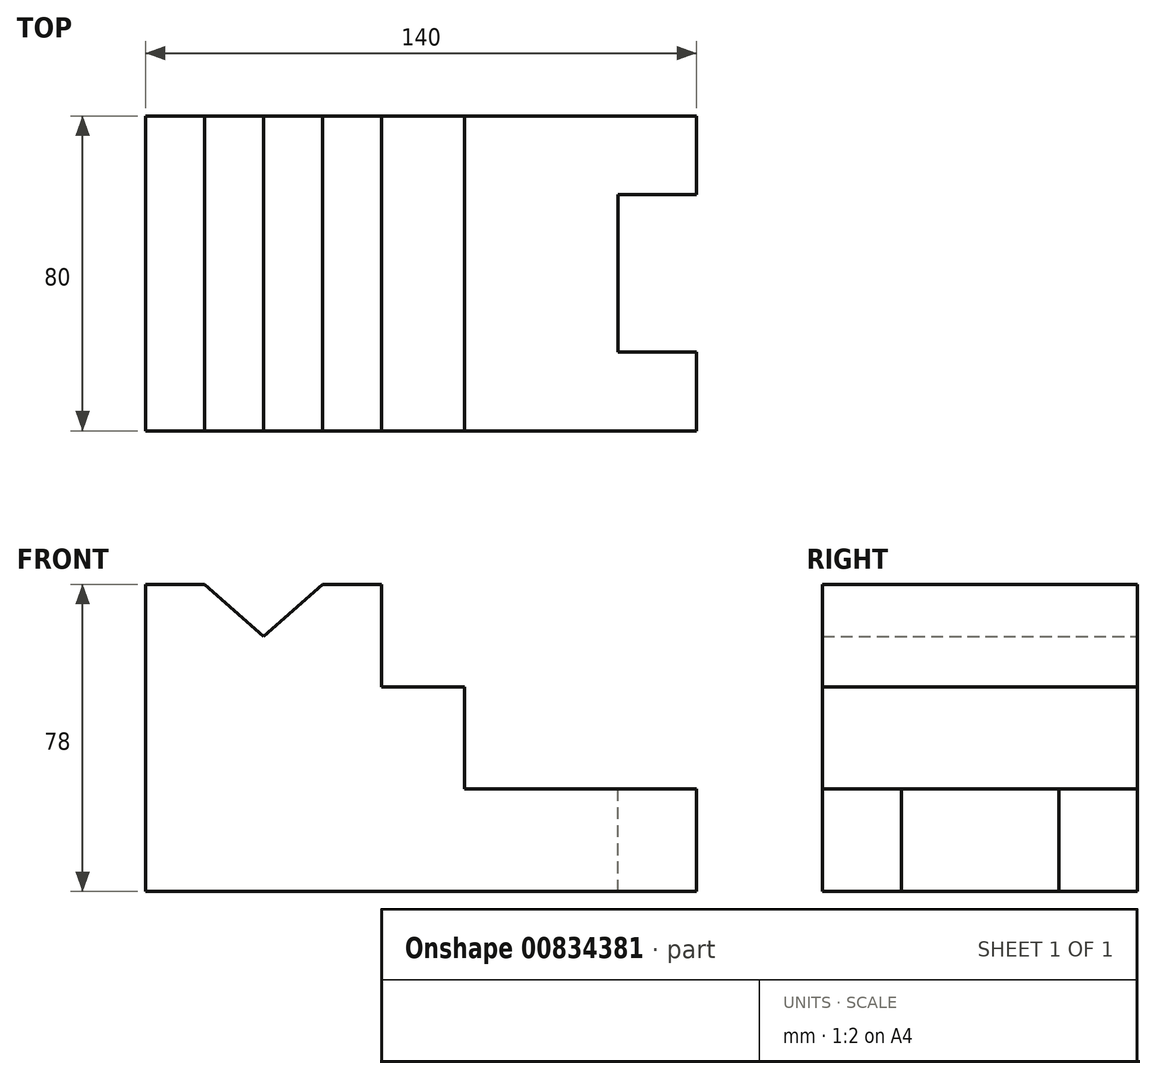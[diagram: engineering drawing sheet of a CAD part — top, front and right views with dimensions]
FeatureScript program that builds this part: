
annotation { "Feature Type Name" : "Feature", "Feature Type Description" : "" }
export const myFeature = defineFeature(function(context is Context, id is Id, definition is map)
    precondition{}
    {
        {
            var Q0;
            Q0=qCreatedBy(makeId("Front.planeOp"),FACE);
            var sketch = newSketch(context, id + "F0", { "sketchPlane" : qUnion([Q0])});
            skLineSegment(sketch, "E0", {"start": v(57.57, -14.86) * mm, "end": v(-82.43, -14.86) * mm});
            skLineSegment(sketch, "E1", {"start": v(-82.43, -14.86) * mm, "end": v(-82.43, 63.14) * mm});
            skLineSegment(sketch, "E2", {"start": v(-82.43, 63.14) * mm, "end": v(-67.43, 63.14) * mm});
            skLineSegment(sketch, "E3", {"start": v(-37.43, 63.14) * mm, "end": v(-22.43, 63.14) * mm});
            skLineSegment(sketch, "E4", {"start": v(-22.43, 63.14) * mm, "end": v(-22.43, 37.14) * mm});
            skLineSegment(sketch, "E5", {"start": v(-22.43, 37.14) * mm, "end": v(-1.45, 37.14) * mm});
            skLineSegment(sketch, "E6", {"start": v(-1.45, 37.14) * mm, "end": v(-1.45, 11.14) * mm});
            skLineSegment(sketch, "E7", {"start": v(-1.45, 11.14) * mm, "end": v(57.57, 11.14) * mm});
            skLineSegment(sketch, "E8", {"start": v(57.57, 11.14) * mm, "end": v(57.57, -14.86) * mm});
            skLineSegment(sketch, "E9", {"start": v(-67.43, 63.14) * mm, "end": v(-52.43, 49.9) * mm});
            skLineSegment(sketch, "E10", {"start": v(-52.43, 49.9) * mm, "end": v(-37.43, 63.14) * mm});
            skSolve(sketch);
        }
        {
            var Q0;
            Q0=makeQuery(id+"F0.imprint","IMPRINT",FACE,{"disambiguationData":[TD([[makeQuery(id+"F0.imprint","IMPRINT",EDGE,{"derivedFrom":sQuery(id+"F0.wireOp",EDGE,"E0")}),-1.0]])]});
            extrude(context, id + "F1", {"entities" : qUnion([Q0]), "depth" : 80 * mm, "offsetDistance" : 25 * mm});
        }
        {
            var Q0;
            Q0=makeQuery(id+"F1.opExtrude","SWEPT_FACE",FACE,{"disambiguationData":[OSD([sQuery(id+"F0.wireOp",EDGE,"E8")])]});
            var sketch = newSketch(context, id + "F2", { "sketchPlane" : qUnion([Q0])});
            skLineSegment(sketch, "E11.bottom", {"start": v(-20, -14.86) * mm, "end": v(-60, -14.86) * mm});
            skLineSegment(sketch, "E11.top", {"start": v(-20, 11.14) * mm, "end": v(-60, 11.14) * mm});
            skLineSegment(sketch, "E11.left", {"start": v(-20, -14.86) * mm, "end": v(-20, 11.14) * mm});
            skLineSegment(sketch, "E11.right", {"start": v(-60, -14.86) * mm, "end": v(-60, 11.14) * mm});
            skSolve(sketch);
        }
        {
            var Q0;
            Q0=makeQuery(id+"F2.imprint","IMPRINT",FACE,{"disambiguationData":[TD([[makeQuery(id+"F2.imprint","IMPRINT",EDGE,{"derivedFrom":sQuery(id+"F2.wireOp",EDGE,"E11.bottom")}),1.0]])]});
            extrude(context, id + "F3", {"entities" : qUnion([Q0]), "operationType" : NewBodyOperationType.REMOVE, "oppositeDirection" : true, "depth" : 20 * mm, "offsetDistance" : 25 * mm});
        }
    });
